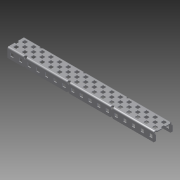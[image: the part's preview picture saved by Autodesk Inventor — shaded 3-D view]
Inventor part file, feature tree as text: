
AUTODESK INVENTOR PART (.ipt)
format: ipt  version: 2014 SP1 (Build 180222100, 222)  size: 1,492,480 bytes
history: native  units: in
note: dims shown in document units (in); Inventor stores cm internally (conversion verified against a paired STEP export)
features: other x1, imported_body x1, extrude x1, sketch x1
ambient origin geometry x8: Origin, YZ Plane, XZ Plane, XY Plane, X Axis, Y Axis, Z Axis, Center Point
bodies: Body1 (feature_tree)
feature tree (4):
  parser-record x1  (decoder bookkeeping rows leaked as tree rows — omitted from the tree; the rows remain in map.json)
  imported_body  "Base1"
  extrude  "Extrusion1"  Depth=1.5in
  sketch  "Sketch1"  dims[d0=2.5in d1=1.5in d2=1.0in d3=0.0in]
